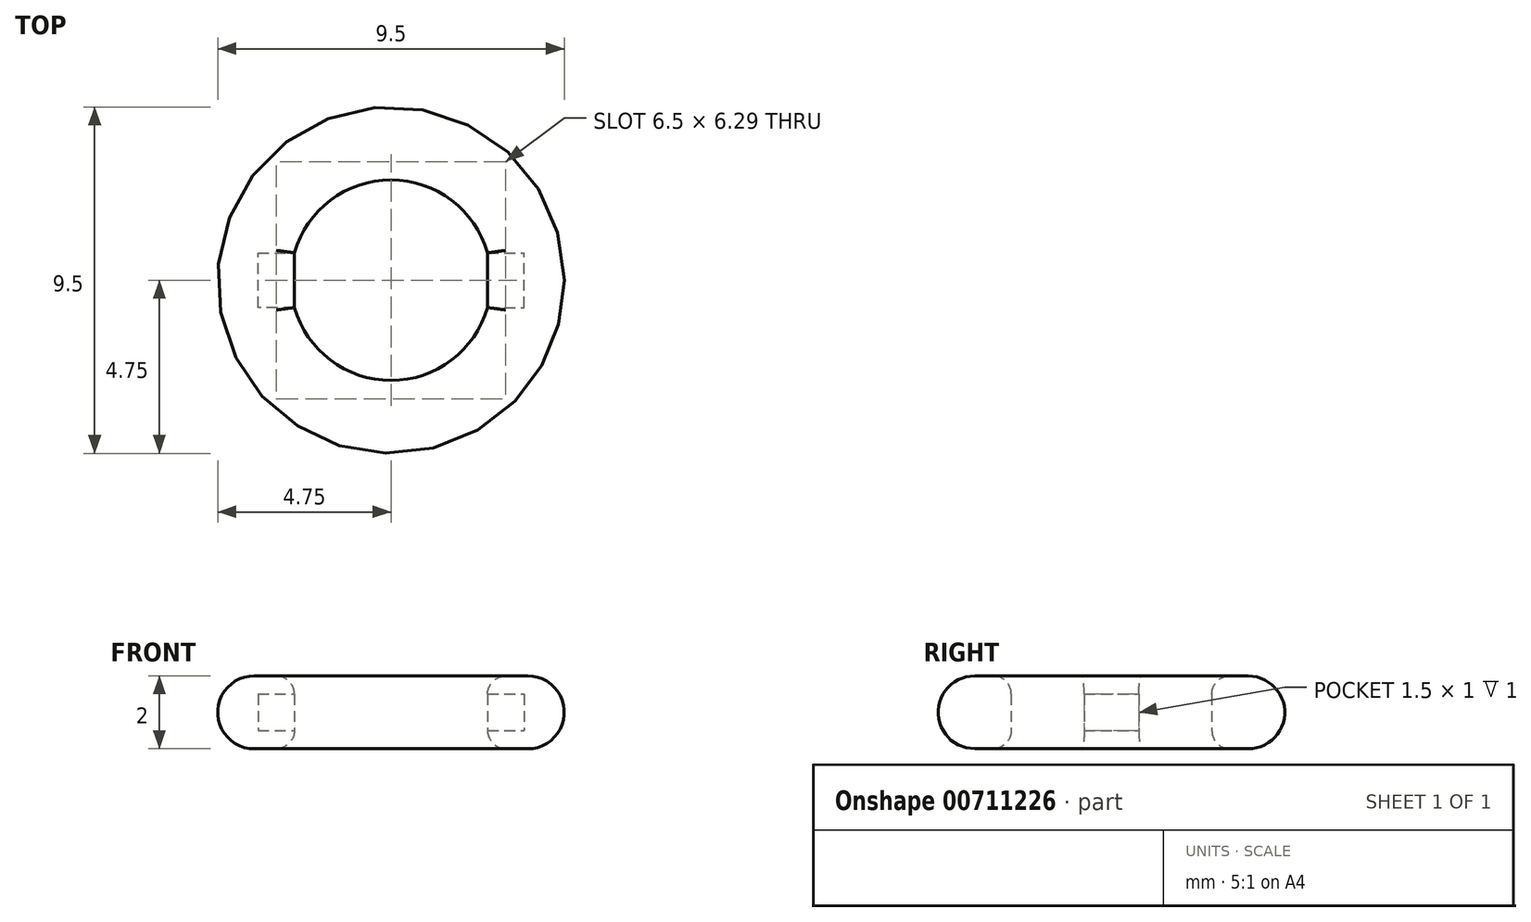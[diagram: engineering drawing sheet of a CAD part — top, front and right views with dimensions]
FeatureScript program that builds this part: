
annotation { "Feature Type Name" : "Feature", "Feature Type Description" : "" }
export const myFeature = defineFeature(function(context is Context, id is Id, definition is map)
    precondition{}
    {
        {
            var Q0;
            Q0=qCreatedBy(makeId("Top.planeOp"),FACE);
            var sketch = newSketch(context, id + "F0", { "sketchPlane" : qUnion([Q0])});
            skArc(sketch, "E0", {"start": v(2.65, 0.75) * mm, "mid": v(0, 2.75) * mm, "end": v(-2.65, 0.75) * mm});
            skCircle(sketch, "E1", {"center": v(0, 0) * mm, "radius": 4.75 * mm});
            skLineSegment(sketch, "E2.bottom", {"start": v(2.65, 0.75) * mm, "end": v(3.65, 0.75) * mm});
            skLineSegment(sketch, "E2.top", {"start": v(2.65, -0.75) * mm, "end": v(3.65, -0.75) * mm});
            skLineSegment(sketch, "E2.right", {"start": v(3.65, 0.75) * mm, "end": v(3.65, -0.75) * mm});
            skLineSegment(sketch, "E3.MirrorCS", {"start": v(-2.65, 0.75) * mm, "end": v(-3.65, 0.75) * mm});
            skLineSegment(sketch, "E4.MirrorCS", {"start": v(-2.65, -0.75) * mm, "end": v(-3.65, -0.75) * mm});
            skLineSegment(sketch, "E5.MirrorCS", {"start": v(-3.65, 0.75) * mm, "end": v(-3.65, -0.75) * mm});
            skArc(sketch, "E6.trimOffspring", {"start": v(-2.65, -0.75) * mm, "mid": v(0, -2.75) * mm, "end": v(2.65, -0.75) * mm});
            skSolve(sketch);
        }
        {
            var Q0;
            Q0=makeQuery(id+"F0.imprint","IMPRINT",FACE,{"disambiguationData":[TD([[makeQuery(id+"F0.imprint","IMPRINT",EDGE,{"derivedFrom":sQuery(id+"F0.wireOp",EDGE,"E0")}),-1.0]])]});
            extrude(context, id + "F1", {"entities" : qUnion([Q0]), "depth" : 2 * mm, "offsetDistance" : 25.4 * mm});
        }
        {
            var Q0;
            Q0=makeQuery(id+"F1.opExtrude","SWEPT_FACE",FACE,{"disambiguationData":[OSD([sQuery(id+"F0.wireOp",EDGE,"E3.MirrorCS")])]});
            var sketch = newSketch(context, id + "F2", { "sketchPlane" : qUnion([Q0])});
            skLineSegment(sketch, "E7.bottom", {"start": v(-3.65, 2) * mm, "end": v(-2.65, 2) * mm});
            skLineSegment(sketch, "E7.top", {"start": v(-3.65, 1.5) * mm, "end": v(-2.65, 1.5) * mm});
            skLineSegment(sketch, "E7.left", {"start": v(-3.65, 2) * mm, "end": v(-3.65, 1.5) * mm});
            skLineSegment(sketch, "E7.right", {"start": v(-2.65, 2) * mm, "end": v(-2.65, 1.5) * mm});
            skLineSegment(sketch, "E8.bottom", {"start": v(-3.65, 0) * mm, "end": v(-2.65, 0) * mm});
            skLineSegment(sketch, "E8.top", {"start": v(-3.65, 0.5) * mm, "end": v(-2.65, 0.5) * mm});
            skLineSegment(sketch, "E8.left", {"start": v(-3.65, 0) * mm, "end": v(-3.65, 0.5) * mm});
            skLineSegment(sketch, "E8.right", {"start": v(-2.65, 0) * mm, "end": v(-2.65, 0.5) * mm});
            skSolve(sketch);
        }
        {
            var Q0;
            Q0=makeQuery(id+"F1.opExtrude","SWEPT_FACE",FACE,{"disambiguationData":[OSD([sQuery(id+"F0.wireOp",EDGE,"E2.bottom")])]});
            var sketch = newSketch(context, id + "F3", { "sketchPlane" : qUnion([Q0])});
            skLineSegment(sketch, "E9.bottom", {"start": v(2.65, 0) * mm, "end": v(3.65, 0) * mm});
            skLineSegment(sketch, "E9.top", {"start": v(2.65, 0.5) * mm, "end": v(3.65, 0.5) * mm});
            skLineSegment(sketch, "E9.left", {"start": v(2.65, 0) * mm, "end": v(2.65, 0.5) * mm});
            skLineSegment(sketch, "E9.right", {"start": v(3.65, 0) * mm, "end": v(3.65, 0.5) * mm});
            skLineSegment(sketch, "E10.bottom", {"start": v(2.65, 2) * mm, "end": v(3.65, 2) * mm});
            skLineSegment(sketch, "E10.top", {"start": v(2.65, 1.5) * mm, "end": v(3.65, 1.5) * mm});
            skLineSegment(sketch, "E10.left", {"start": v(2.65, 2) * mm, "end": v(2.65, 1.5) * mm});
            skLineSegment(sketch, "E10.right", {"start": v(3.65, 2) * mm, "end": v(3.65, 1.5) * mm});
            skSolve(sketch);
        }
        {
            var Q0;
            Q0 = qSketchRegion(id + "F2", true);
            var Q1;
            Q1 = qSketchRegion(id + "F3", true);
            extrude(context, id + "F4", {"entities" : qUnion([Q0, Q1]), "operationType" : NewBodyOperationType.ADD, "depth" : 2.5 * mm, "offsetDistance" : 25.4 * mm});
        }
        {
            var Q0;
            Q0=makeQuery(id+"F4.opExtrude","SWEPT_EDGE",EDGE,{"disambiguationData":[OSD([sQuery(id+"F2.wireOp",EDGE,"E7.bottom"),sQuery(id+"F2.wireOp",EDGE,"E7.right")])]});
            var Q1;
            Q1=makeQuery(id+"F4.opExtrude","SWEPT_EDGE",EDGE,{"disambiguationData":[OSD([sQuery(id+"F3.wireOp",EDGE,"E10.bottom"),sQuery(id+"F3.wireOp",EDGE,"E10.left")])]});
            var Q2;
            Q2=makeQuery(id+"F1.opExtrude","CAP_EDGE",EDGE,{"disambiguationData":[OSD([sQuery(id+"F0.wireOp",EDGE,"E0")])],"isStart":false});
            var Q3;
            Q3=makeQuery(id+"F1.opExtrude","CAP_EDGE",EDGE,{"disambiguationData":[OSD([sQuery(id+"F0.wireOp",EDGE,"E6.trimOffspring")])],"isStart":false});
            var Q4;
            Q4=makeQuery(id+"F1.opExtrude","CAP_EDGE",EDGE,{"disambiguationData":[OSD([sQuery(id+"F0.wireOp",EDGE,"E0")])],"isStart":true});
            var Q5;
            Q5=makeQuery(id+"F1.opExtrude","CAP_EDGE",EDGE,{"disambiguationData":[OSD([sQuery(id+"F0.wireOp",EDGE,"E6.trimOffspring")])],"isStart":true});
            var Q6;
            Q6=makeQuery(id+"F4.opExtrude","SWEPT_EDGE",EDGE,{"disambiguationData":[OSD([sQuery(id+"F2.wireOp",EDGE,"E8.bottom"),sQuery(id+"F2.wireOp",EDGE,"E8.right")])]});
            var Q7;
            Q7=makeQuery(id+"F4.opExtrude","SWEPT_EDGE",EDGE,{"disambiguationData":[OSD([sQuery(id+"F3.wireOp",EDGE,"E9.bottom"),sQuery(id+"F3.wireOp",EDGE,"E9.left")])]});
            fillet(context, id + "F5", {"entities" : qUnion([Q0, Q1, Q2, Q3, Q4, Q5, Q6, Q7]), "radius" : .5 * mm, "tangentPropagation" : true, "allowEdgeOverflow" : false});
        }
        {
            var Q0;
            Q0=makeQuery(id+"F1.opExtrude","CAP_EDGE",EDGE,{"disambiguationData":[OSD([sQuery(id+"F0.wireOp",EDGE,"E1")])],"isStart":false});
            var Q1;
            Q1=makeQuery(id+"F1.opExtrude","CAP_EDGE",EDGE,{"disambiguationData":[OSD([sQuery(id+"F0.wireOp",EDGE,"E1")])],"isStart":true});
            fillet(context, id + "F6", {"entities" : qUnion([Q0, Q1]), "radius" : 1 * mm, "tangentPropagation" : true, "allowEdgeOverflow" : false});
        }
    });
